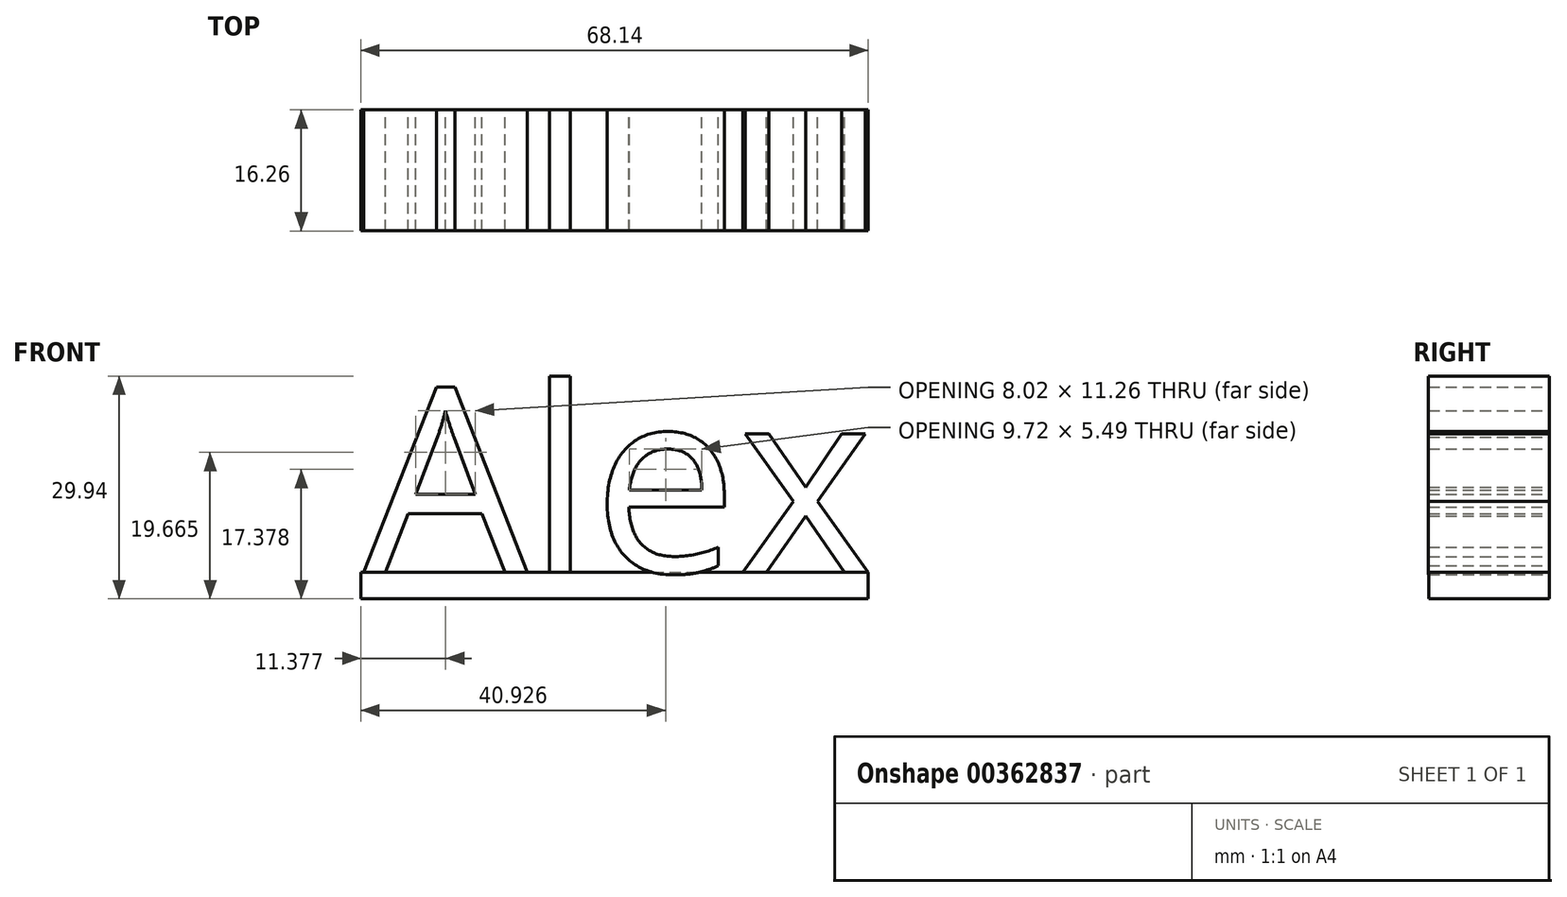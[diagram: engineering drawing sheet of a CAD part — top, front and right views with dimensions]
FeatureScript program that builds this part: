
annotation { "Feature Type Name" : "Feature", "Feature Type Description" : "" }
export const myFeature = defineFeature(function(context is Context, id is Id, definition is map)
    precondition{}
    {
        {
            var Q0;
            Q0=qCreatedBy(makeId("Front.planeOp"),FACE);
            var sketch = newSketch(context, id + "F0", { "sketchPlane" : qUnion([Q0])});
            skText(sketch, "E0", { "text": "Alex\n", "fontName": "OpenSans-Regular.ttf"});
            const initialGuessF0  = {"E0": [-0.03456, 0, 1, 0, 0.025]};
            skSetInitialGuess(sketch, initialGuessF0);
            skSolve(sketch);
        }
        {
            var Q0;
            Q0 = qSketchRegion(id + "F0", true);
            extrude(context, id + "F1", {"entities" : qUnion([Q0]), "depth" : 16.26 * mm});
        }
        {
            var Q0;
            Q0=qCreatedBy(makeId("Top.planeOp"),FACE);
            var sketch = newSketch(context, id + "F2", { "sketchPlane" : qUnion([Q0])});
            skLineSegment(sketch, "E1.bottom", {"start": v(-34.94, 0) * mm, "end": v(33.2, 0) * mm});
            skLineSegment(sketch, "E1.top", {"start": v(-34.94, -16.24) * mm, "end": v(33.2, -16.24) * mm});
            skLineSegment(sketch, "E1.left", {"start": v(-34.94, 0) * mm, "end": v(-34.94, -16.24) * mm});
            skLineSegment(sketch, "E1.right", {"start": v(33.2, 0) * mm, "end": v(33.2, -16.24) * mm});
            skSolve(sketch);
        }
        {
            var Q0;
            Q0=makeQuery(id+"F2.imprint","IMPRINT",FACE,{"disambiguationData":[TD([[makeQuery(id+"F2.imprint","IMPRINT",EDGE,{"derivedFrom":sQuery(id+"F2.wireOp",EDGE,"E1.bottom")}),-1.0]])]});
            extrude(context, id + "F3", {"entities" : qUnion([Q0]), "oppositeDirection" : true, "depth" : 3.56 * mm});
        }
    });
